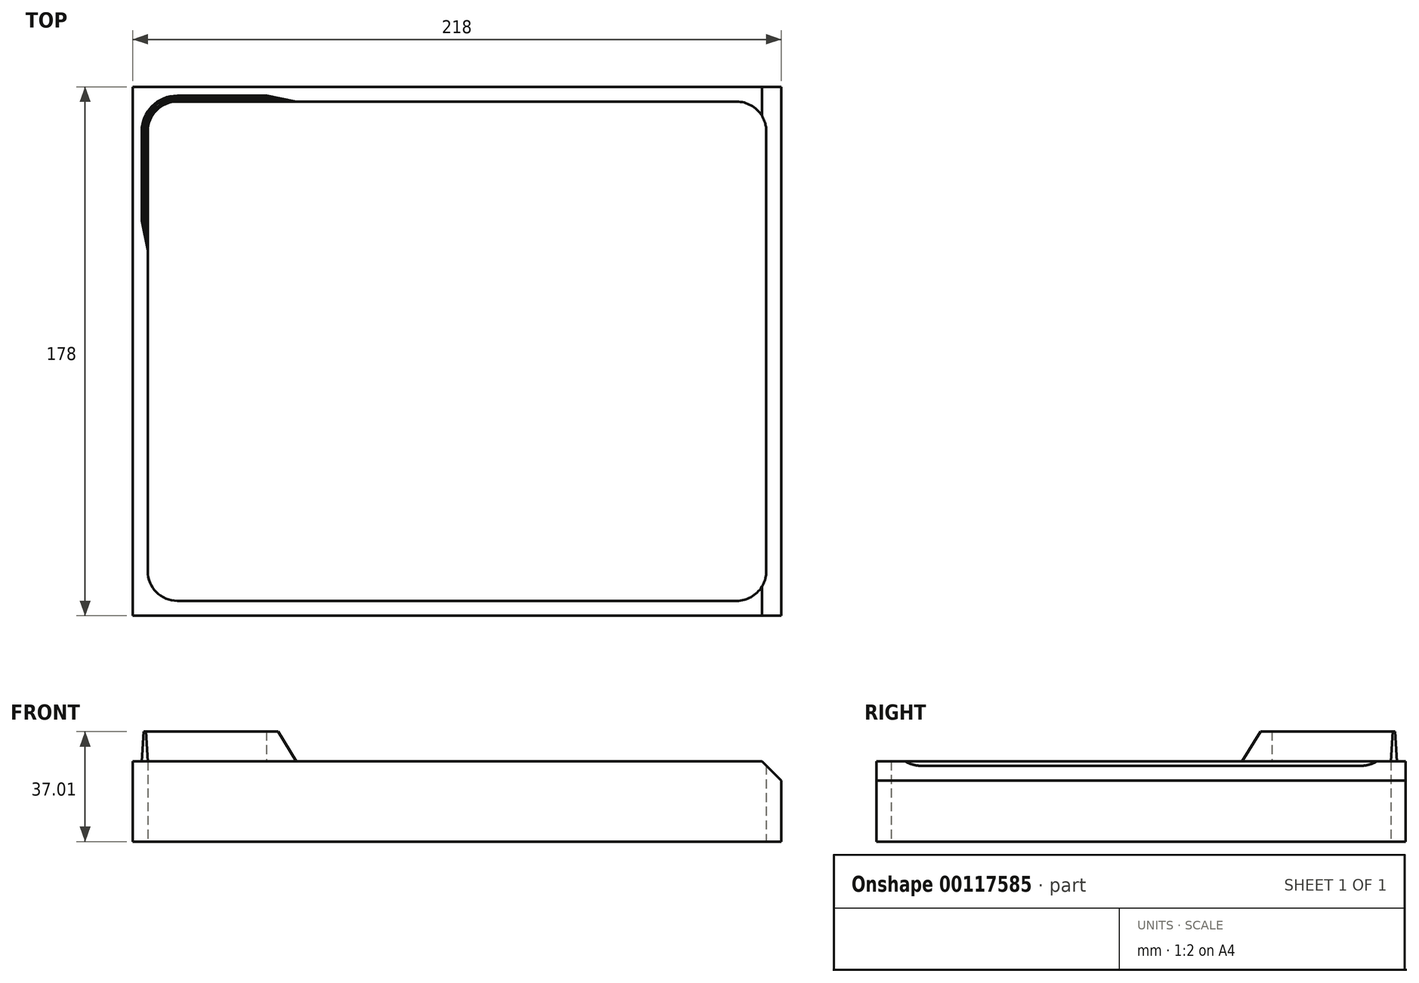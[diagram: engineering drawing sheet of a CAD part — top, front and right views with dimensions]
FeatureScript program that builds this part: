
annotation { "Feature Type Name" : "Feature", "Feature Type Description" : "" }
export const myFeature = defineFeature(function(context is Context, id is Id, definition is map)
    precondition{}
    {
        {
            var Q0;
            Q0=qCreatedBy(makeId("Top.planeOp"),FACE);
            var sketch = newSketch(context, id + "F0", { "sketchPlane" : qUnion([Q0])});
            skLineSegment(sketch, "E0.bottom", {"start": v(-97.32, 82.2) * mm, "end": v(90.68, 82.2) * mm});
            skLineSegment(sketch, "E0.top", {"start": v(-97.32, -85.8) * mm, "end": v(90.68, -85.8) * mm});
            skLineSegment(sketch, "E0.left", {"start": v(-107.32, 72.2) * mm, "end": v(-107.32, -75.8) * mm});
            skLineSegment(sketch, "E0.right", {"start": v(100.68, 72.2) * mm, "end": v(100.68, -75.8) * mm});
            skArc(sketch, "E1.filletArc", {"start": v(-97.32, 82.2) * mm, "mid": v(-104.4, 79.27) * mm, "end": v(-107.32, 72.2) * mm});
            skArc(sketch, "E2.filletArc", {"start": v(100.68, 72.2) * mm, "mid": v(97.75, 79.27) * mm, "end": v(90.68, 82.2) * mm});
            skArc(sketch, "E3.filletArc", {"start": v(90.68, -85.8) * mm, "mid": v(97.75, -82.87) * mm, "end": v(100.68, -75.8) * mm});
            skArc(sketch, "E4.filletArc", {"start": v(-107.32, -75.8) * mm, "mid": v(-104.4, -82.87) * mm, "end": v(-97.32, -85.8) * mm});
            skLineSegment(sketch, "E5.0", {"start": v(-112.32, -90.8) * mm, "end": v(105.68, -90.8) * mm});
            skLineSegment(sketch, "E5.3", {"start": v(-112.32, 87.2) * mm, "end": v(-112.32, -90.8) * mm});
            skLineSegment(sketch, "E5.4", {"start": v(105.68, 87.2) * mm, "end": v(105.68, -90.8) * mm});
            skLineSegment(sketch, "E5.6", {"start": v(-112.32, 87.2) * mm, "end": v(105.68, 87.2) * mm});
            skLineSegment(sketch, "E6.bottom", {"start": v(-54.32, 35.2) * mm, "end": v(47.68, 35.2) * mm, "construction": true});
            skLineSegment(sketch, "E6.top", {"start": v(-54.32, -38.8) * mm, "end": v(47.68, -38.8) * mm, "construction": true});
            skLineSegment(sketch, "E6.left", {"start": v(-54.32, 35.2) * mm, "end": v(-54.32, -38.8) * mm, "construction": true});
            skLineSegment(sketch, "E6.right", {"start": v(47.68, 35.2) * mm, "end": v(47.68, -38.8) * mm, "construction": true});
            skLineSegment(sketch, "E7", {"start": v(-3.32, 82.2) * mm, "end": v(-3.32, -158.19) * mm, "construction": true});
            skLineSegment(sketch, "E8", {"start": v(105.68, 77.2) * mm, "end": v(110.68, 77.2) * mm});
            skLineSegment(sketch, "E9", {"start": v(120.68, 67.2) * mm, "end": v(120.68, -80.8) * mm});
            skLineSegment(sketch, "E10", {"start": v(110.68, -90.8) * mm, "end": v(105.68, -90.8) * mm});
            skPoint(sketch, "E11.visualSharp", {"position": v(120.68, 77.2) * mm});
            skArc(sketch, "E11.filletArc", {"start": v(120.68, 67.2) * mm, "mid": v(117.75, 74.27) * mm, "end": v(110.68, 77.2) * mm});
            skPoint(sketch, "E12.visualSharp", {"position": v(120.68, -90.8) * mm});
            skArc(sketch, "E12.filletArc", {"start": v(110.68, -90.8) * mm, "mid": v(117.75, -87.87) * mm, "end": v(120.68, -80.8) * mm});
            skSolve(sketch);
        }
        {
            var Q0;
            Q0=makeQuery(id+"F0.imprint","IMPRINT",FACE,{"disambiguationData":[TD([[makeQuery(id+"F0.imprint","IMPRINT",EDGE,{"derivedFrom":sQuery(id+"F0.wireOp",EDGE,"E0.bottom")}),1.0]])]});
            extrude(context, id + "F1", {"entities" : qUnion([Q0]), "depth" : 27 * mm});
        }
        {
            var Q0;
            Q0=makeQuery(id+"F1.opExtrude","CAP_EDGE",EDGE,{"disambiguationData":[OSD([sQuery(id+"F0.wireOp",EDGE,"E5.4")])],"isStart":false});
            chamfer(context, id + "F2", {"entities" : qUnion([Q0]), "width" : 6.5 * mm});
        }
        {
            var Q0;
            Q0=makeQuery(id+"F0.imprint","IMPRINT",FACE,{"disambiguationData":[TD([[makeQuery(id+"F0.imprint","IMPRINT",EDGE,{"derivedFrom":sQuery(id+"F0.wireOp",EDGE,"E0.bottom")}),-1.0]])]});
            var Q1;
            Q1=makeQuery(id+"F0.imprint","IMPRINT",FACE,{"disambiguationData":[TD([[makeQuery(id+"F0.imprint","IMPRINT",EDGE,{"derivedFrom":sQuery(id+"F0.wireOp",EDGE,"E0.bottom")}),1.0]])]});
            var Q2;
            Q2=makeQuery(id+"F0.imprint","IMPRINT",FACE,{"disambiguationData":[TD([[makeQuery(id+"F0.imprint","IMPRINT",EDGE,{"derivedFrom":sQuery(id+"F0.wireOp",EDGE,"E5.2")}),-1.0]])]});
            extrude(context, id + "F3", {"entities" : qUnion([Q0, Q1, Q2]), "oppositeDirection" : true, "depth" : 3 / 406.4 * mm});
        }
        {
            var Q0;
            Q0=makeQuery(id+"F1.opExtrude","CAP_FACE",FACE,{"disambiguationData":[OSD([sQuery(id+"F0.wireOp",EDGE,"E0.bottom"),sQuery(id+"F0.wireOp",EDGE,"E0.top"),sQuery(id+"F0.wireOp",EDGE,"E0.left"),sQuery(id+"F0.wireOp",EDGE,"E0.right"),sQuery(id+"F0.wireOp",EDGE,"E1.filletArc"),sQuery(id+"F0.wireOp",EDGE,"E2.filletArc"),sQuery(id+"F0.wireOp",EDGE,"E3.filletArc"),sQuery(id+"F0.wireOp",EDGE,"E4.filletArc"),sQuery(id+"F0.wireOp",EDGE,"E5.0"),sQuery(id+"F0.wireOp",EDGE,"E5.3"),sQuery(id+"F0.wireOp",EDGE,"E5.4"),sQuery(id+"F0.wireOp",EDGE,"E5.6")])],"isStart":false});
            var sketch = newSketch(context, id + "F4", { "sketchPlane" : qUnion([Q0])});
            skArc(sketch, "E13.0", {"start": v(-97.32, 82.2) * mm, "mid": v(-104.4, 79.27) * mm, "end": v(-107.32, 72.2) * mm});
            skArc(sketch, "E14.0", {"start": v(-97.32, 84.2) * mm, "mid": v(-105.8, 80.69) * mm, "end": v(-109.32, 72.2) * mm});
            skLineSegment(sketch, "E15", {"start": v(-97.32, 82.2) * mm, "end": v(-57.32, 82.2) * mm});
            skLineSegment(sketch, "E16", {"start": v(-107.32, 72.2) * mm, "end": v(-107.32, 32.2) * mm});
            skLineSegment(sketch, "E17", {"start": v(-109.32, 72.2) * mm, "end": v(-109.32, 42.2) * mm});
            skLineSegment(sketch, "E18", {"start": v(-109.32, 42.2) * mm, "end": v(-107.32, 32.2) * mm});
            skLineSegment(sketch, "E19", {"start": v(-97.32, 84.2) * mm, "end": v(-67.32, 84.2) * mm});
            skLineSegment(sketch, "E20", {"start": v(-67.32, 84.2) * mm, "end": v(-57.32, 82.2) * mm});
            skSolve(sketch);
        }
        {
            var Q0;
            Q0=makeQuery(id+"F4.imprint","IMPRINT",FACE,{"disambiguationData":[TD([[makeQuery(id+"F4.imprint","IMPRINT",EDGE,{"derivedFrom":sQuery(id+"F4.wireOp",EDGE,"E13.0")}),-1.0]])]});
            extrude(context, id + "F5", {"entities" : qUnion([Q0]), "operationType" : NewBodyOperationType.ADD, "depth" : 10 * mm, "hasDraft" : true, "draftAngle" : 3.5 * degree, "draftPullDirection" : true});
        }
    });
